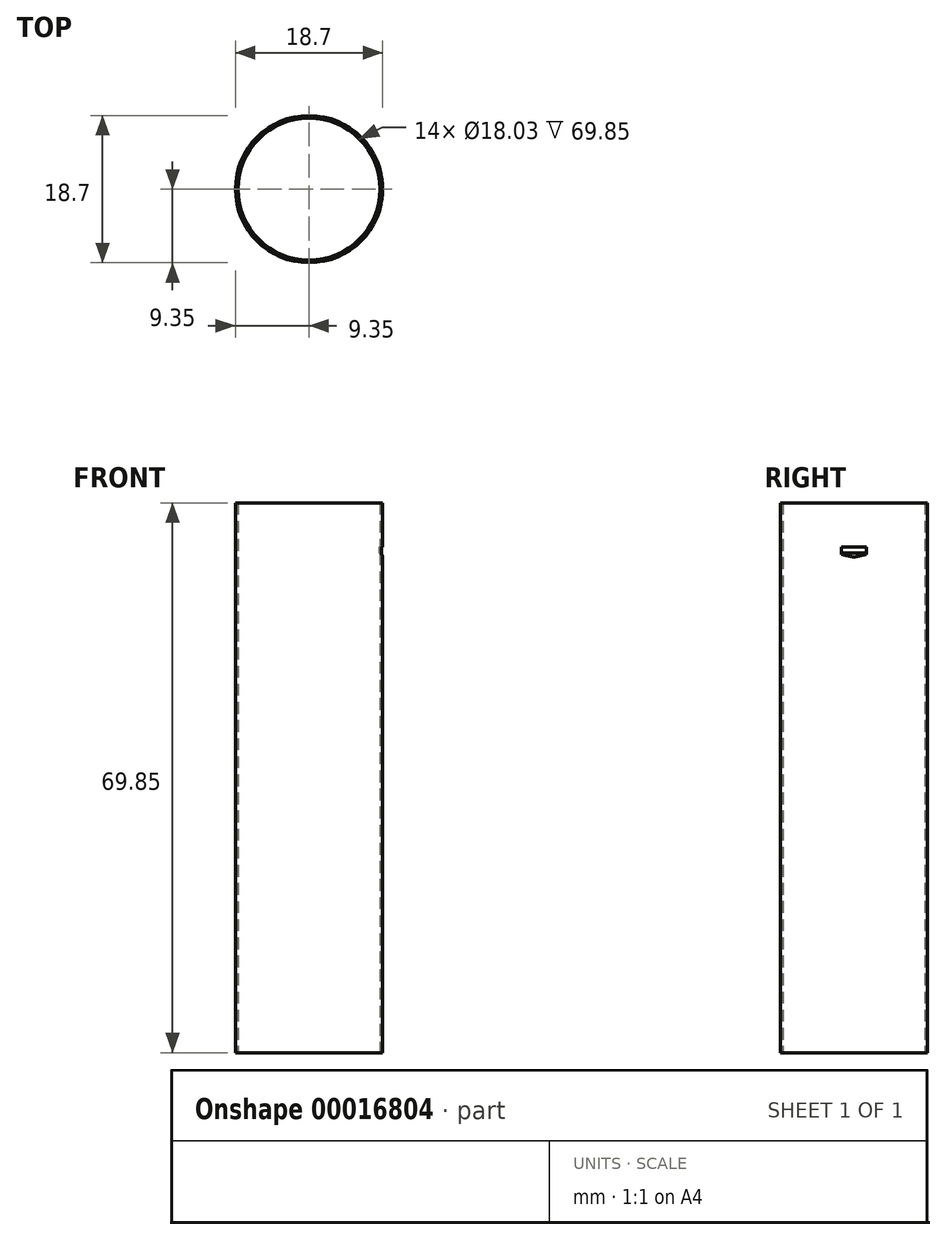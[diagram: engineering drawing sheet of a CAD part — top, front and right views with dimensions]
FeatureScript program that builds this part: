
annotation { "Feature Type Name" : "Feature", "Feature Type Description" : "" }
export const myFeature = defineFeature(function(context is Context, id is Id, definition is map)
    precondition{}
    {
        {
            var Q0;
            Q0=qCreatedBy(makeId("Front.planeOp"),FACE);
            var sketch = newSketch(context, id + "F0", { "sketchPlane" : qUnion([Q0])});
            skLineSegment(sketch, "E0", {"start": v(0, 0) * mm, "end": v(9.02, 0) * mm});
            skLineSegment(sketch, "E1", {"start": v(9.02, 0) * mm, "end": v(9.02, 69.85) * mm});
            skLineSegment(sketch, "E2", {"start": v(9.02, 69.85) * mm, "end": v(9.35, 69.85) * mm});
            skLineSegment(sketch, "E3", {"start": v(9.35, 69.85) * mm, "end": v(9.35, 0) * mm});
            skLineSegment(sketch, "E4", {"start": v(9.35, 0) * mm, "end": v(9.02, 0) * mm});
            skLineSegment(sketch, "E5", {"start": v(0, 0) * mm, "end": v(0, 69.85) * mm});
            skLineSegment(sketch, "E6", {"start": v(0, 69.85) * mm, "end": v(9.02, 69.85) * mm});
            skSolve(sketch);
        }
        {
            var Q0;
            Q0=makeQuery(id+"F0.imprint","IMPRINT",FACE,{"disambiguationData":[TD([[makeQuery(id+"F0.imprint","IMPRINT",EDGE,{"derivedFrom":sQuery(id+"F0.wireOp",EDGE,"E1")}),-1.0]])]});
            var Q1;
            Q1=sQuery(id+"F0.wireOp",EDGE,"E5");
            revolve(context, id + "F1", {"entities" : qUnion([Q0]), "axis" : qUnion([Q1]), "revolveType" : RevolveType.FULL});
        }
        {
            var Q0;
            Q0=qCreatedBy(makeId("Front.planeOp"),FACE);
            var sketch = newSketch(context, id + "F2", { "sketchPlane" : qUnion([Q0])});
            skLineSegment(sketch, "E7", {"start": v(6.25, 64.21) * mm, "end": v(10.06, 64.21) * mm});
            skLineSegment(sketch, "E8", {"start": v(10.06, 64.21) * mm, "end": v(10.06, -7.44) * mm});
            skLineSegment(sketch, "E9", {"start": v(10.06, -7.44) * mm, "end": v(6.25, -7.44) * mm});
            skLineSegment(sketch, "E10", {"start": v(6.25, -7.44) * mm, "end": v(6.25, 64.21) * mm, "construction": true});
            skLineSegment(sketch, "E11.0", {"start": v(9.35, 69.85) * mm, "end": v(9.35, 0) * mm});
            skArc(sketch, "E12", {"start": v(10.06, 62.94) * mm, "mid": v(9.69, 63.84) * mm, "end": v(8.79, 64.21) * mm});
            skArc(sketch, "E13", {"start": v(8.79, -7.44) * mm, "mid": v(9.69, -7.07) * mm, "end": v(10.06, -6.17) * mm});
            skArc(sketch, "E14.0", {"start": v(8.79, -6.73) * mm, "mid": v(9.18, -6.57) * mm, "end": v(9.35, -6.17) * mm});
            skLineSegment(sketch, "E15", {"start": v(8.79, -6.73) * mm, "end": v(6.25, -6.73) * mm});
            skLineSegment(sketch, "E16", {"start": v(6.25, -6.73) * mm, "end": v(6.25, -7.44) * mm});
            skLineSegment(sketch, "E17", {"start": v(9.35, -6.17) * mm, "end": v(9.35, 62.94) * mm});
            skLineSegment(sketch, "E18", {"start": v(9.35, -6.17) * mm, "end": v(10.06, -6.17) * mm, "construction": true});
            skLineSegment(sketch, "E19", {"start": v(8.79, -7.44) * mm, "end": v(8.79, -6.73) * mm, "construction": true});
            skLineSegment(sketch, "E20", {"start": v(10.06, 62.94) * mm, "end": v(9.35, 62.94) * mm, "construction": true});
            skArc(sketch, "E21", {"start": v(9.35, 62.94) * mm, "mid": v(9.18, 63.34) * mm, "end": v(8.79, 63.5) * mm});
            skLineSegment(sketch, "E22", {"start": v(8.79, 64.21) * mm, "end": v(8.79, 63.5) * mm, "construction": true});
            skLineSegment(sketch, "E23", {"start": v(8.79, 63.5) * mm, "end": v(6.25, 63.5) * mm});
            skLineSegment(sketch, "E24", {"start": v(6.25, 63.5) * mm, "end": v(6.25, 64.21) * mm});
            skSolve(sketch);
        }
        {
            var Q0;
            {var subQ5=sQuery(id+"F2.wireOp",EDGE,"E13");Q0=makeQuery(id+"F2.imprint","IMPRINT",FACE,{"disambiguationData":[TD([[makeQuery(id+"F2.imprint","IMPRINT",EDGE,{"derivedFrom":subQ5}),1.0]])]});}
            var Q1;
            {var subQ1=sQuery(id+"F2.wireOp",EDGE,"E21");Q1=makeQuery(id+"F2.imprint","IMPRINT",FACE,{"disambiguationData":[TD([[makeQuery(id+"F2.imprint","IMPRINT",EDGE,{"derivedFrom":subQ1}),-1.0]])]});}
            var Q2;
            {var subQ3=sQuery(id+"F2.wireOp",EDGE,"E8");var subQ5=sQuery(id+"F2.wireOp",EDGE,"E7");var subQ7=makeQuery(id+"F2.imprint","INTERSECT",VERTEX,{"derivedFrom":[subQ5,subQ3]});Q2=makeQuery(id+"F2.imprint","IMPRINT",FACE,{"disambiguationData":[TD([[makeQuery(id+"F2.imprint","IMPRINT",EDGE,{"disambiguationData":[TD([[subQ7,1.0]])],"derivedFrom":subQ5}),-1.0]])]});}
            var Q3;
            {var subQ0=sQuery(id+"F2.wireOp",EDGE,"E12");var subQ3=sQuery(id+"F2.wireOp",EDGE,"E7");var subQ4=makeQuery(id+"F2.imprint","INTERSECT",VERTEX,{"derivedFrom":[subQ3,subQ0]});Q3=makeQuery(id+"F2.imprint","IMPRINT",FACE,{"disambiguationData":[TD([[makeQuery(id+"F2.imprint","IMPRINT",EDGE,{"disambiguationData":[TD([[subQ4,-1.0]])],"derivedFrom":subQ3}),-1.0]])]});}
            extrude(context, id + "F3", {"entities" : qUnion([Q0, Q1, Q2, Q3]), "operationType" : NewBodyOperationType.REMOVE, "oppositeDirection" : true, "depth" : 3.17 * mm, "symmetric" : true});
        }
    });
